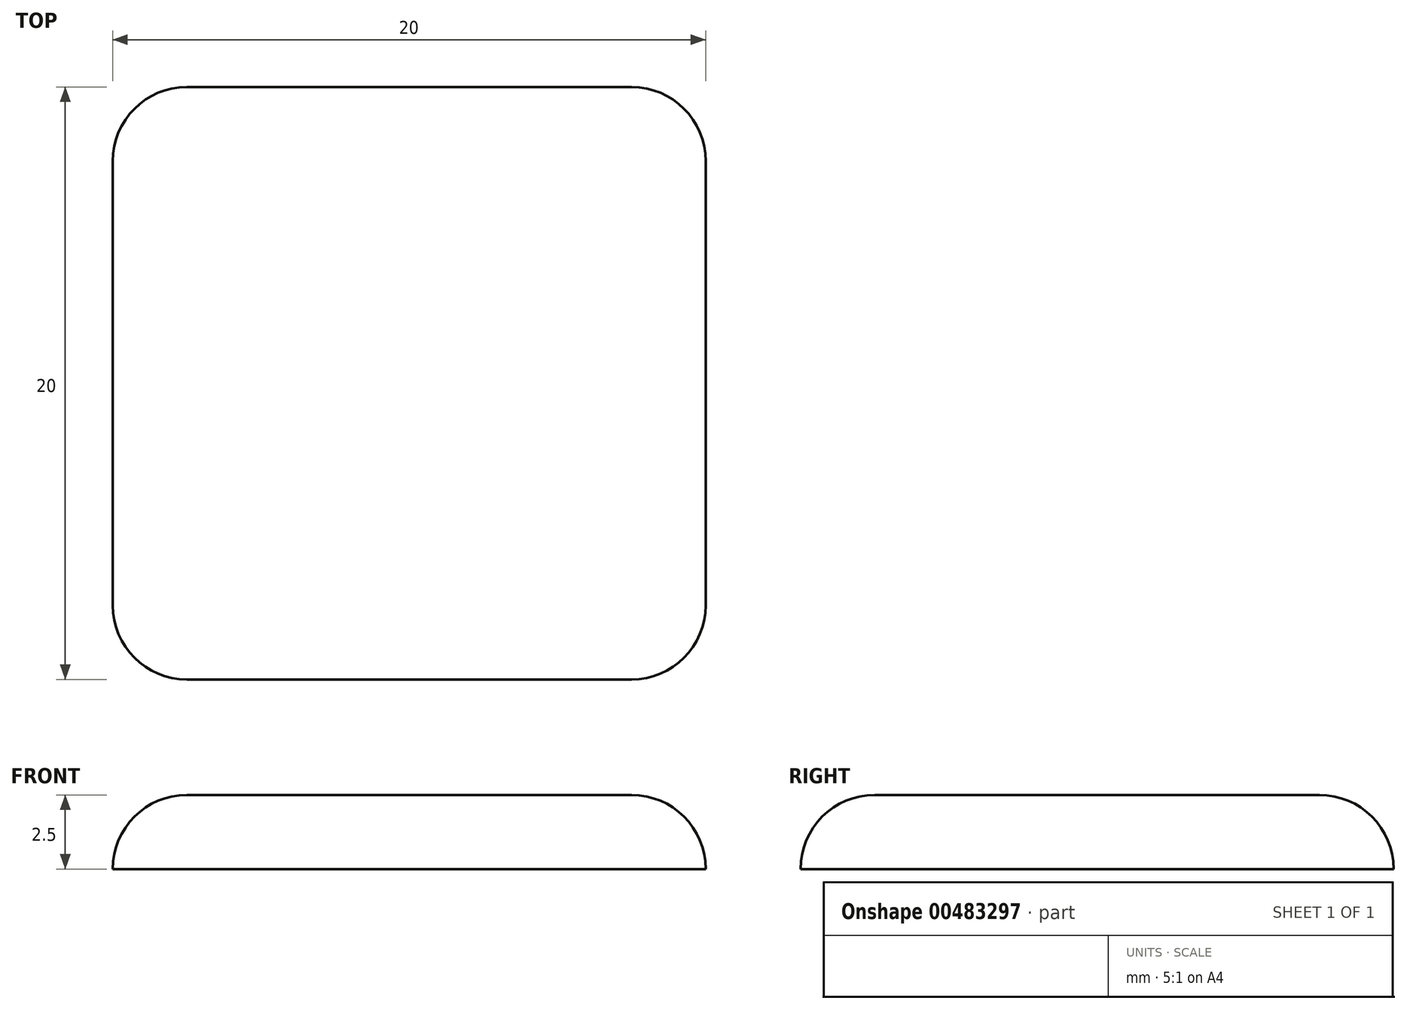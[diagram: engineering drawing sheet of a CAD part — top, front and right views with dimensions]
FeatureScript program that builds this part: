
annotation { "Feature Type Name" : "Feature", "Feature Type Description" : "" }
export const myFeature = defineFeature(function(context is Context, id is Id, definition is map)
    precondition{}
    {
        {
            var Q0;
            Q0=qCreatedBy(makeId("Top.planeOp"),FACE);
            var sketch = newSketch(context, id + "F0", { "sketchPlane" : qUnion([Q0])});
            skLineSegment(sketch, "E0.bottom", {"start": v(10, 10) * mm, "end": v(-10, 10) * mm});
            skLineSegment(sketch, "E0.top", {"start": v(10, -10) * mm, "end": v(-10, -10) * mm});
            skLineSegment(sketch, "E0.left", {"start": v(10, 10) * mm, "end": v(10, -10) * mm});
            skLineSegment(sketch, "E0.right", {"start": v(-10, 10) * mm, "end": v(-10, -10) * mm});
            skPoint(sketch, "E0.middle", {"position": v(0, 0) * mm});
            skSolve(sketch);
        }
        {
            var Q0;
            Q0=makeQuery(id+"F0.imprint","IMPRINT",FACE,{"disambiguationData":[TD([[makeQuery(id+"F0.imprint","IMPRINT",EDGE,{"derivedFrom":sQuery(id+"F0.wireOp",EDGE,"E0.bottom")}),1.0]])]});
            extrude(context, id + "F1", {"entities" : qUnion([Q0]), "depth" : 2.5 * mm});
        }
        {
            var Q0;
            Q0=makeQuery(id+"F1.opExtrude","SWEPT_EDGE",EDGE,{"disambiguationData":[OSD([sQuery(id+"F0.wireOp",EDGE,"E0.top"),sQuery(id+"F0.wireOp",EDGE,"E0.left")])]});
            var Q1;
            Q1=makeQuery(id+"F1.opExtrude","SWEPT_EDGE",EDGE,{"disambiguationData":[OSD([sQuery(id+"F0.wireOp",EDGE,"E0.bottom"),sQuery(id+"F0.wireOp",EDGE,"E0.left")])]});
            var Q2;
            Q2=makeQuery(id+"F1.opExtrude","SWEPT_EDGE",EDGE,{"disambiguationData":[OSD([sQuery(id+"F0.wireOp",EDGE,"E0.top"),sQuery(id+"F0.wireOp",EDGE,"E0.right")])]});
            var Q3;
            Q3=makeQuery(id+"F1.opExtrude","SWEPT_EDGE",EDGE,{"disambiguationData":[OSD([sQuery(id+"F0.wireOp",EDGE,"E0.bottom"),sQuery(id+"F0.wireOp",EDGE,"E0.right")])]});
            var Q4;
            Q4=makeQuery(id+"F1.opExtrude","CAP_EDGE",EDGE,{"disambiguationData":[OSD([sQuery(id+"F0.wireOp",EDGE,"E0.top")])],"isStart":false});
            var Q5;
            Q5=makeQuery(id+"F1.opExtrude","CAP_EDGE",EDGE,{"disambiguationData":[OSD([sQuery(id+"F0.wireOp",EDGE,"E0.left")])],"isStart":false});
            var Q6;
            Q6=makeQuery(id+"F1.opExtrude","CAP_EDGE",EDGE,{"disambiguationData":[OSD([sQuery(id+"F0.wireOp",EDGE,"E0.bottom")])],"isStart":false});
            var Q7;
            Q7=makeQuery(id+"F1.opExtrude","CAP_EDGE",EDGE,{"disambiguationData":[OSD([sQuery(id+"F0.wireOp",EDGE,"E0.right")])],"isStart":false});
            fillet(context, id + "F2", {"entities" : qUnion([Q0, Q1, Q2, Q3, Q4, Q5, Q6, Q7]), "radius" : 2.5 * mm, "tangentPropagation" : true, "allowEdgeOverflow" : false});
        }
    });
